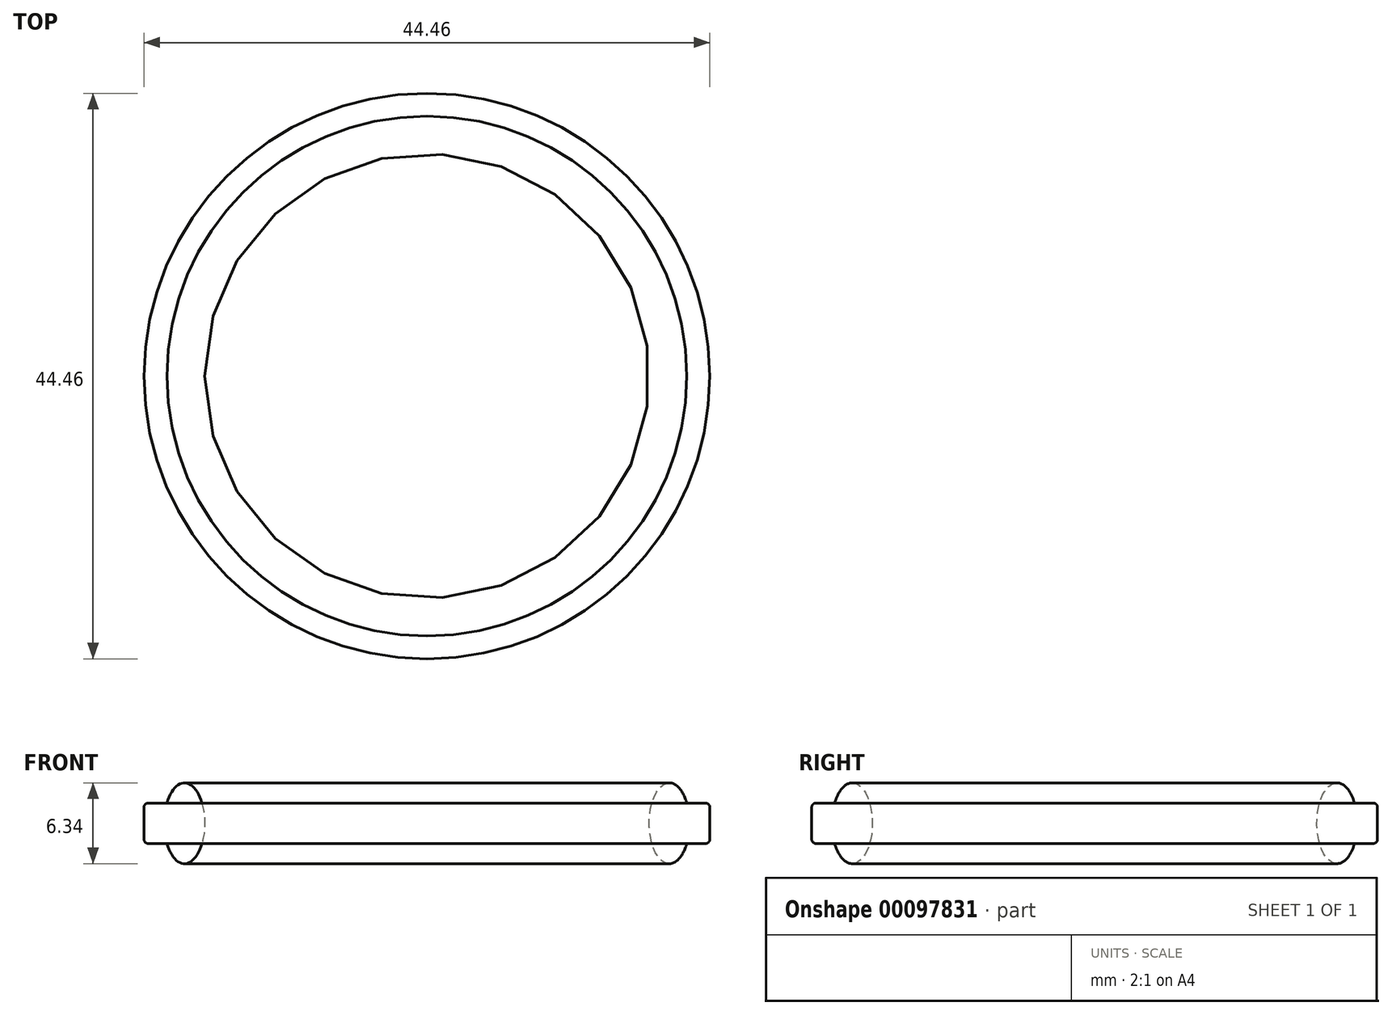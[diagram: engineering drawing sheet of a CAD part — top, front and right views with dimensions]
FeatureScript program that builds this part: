
annotation { "Feature Type Name" : "Feature", "Feature Type Description" : "" }
export const myFeature = defineFeature(function(context is Context, id is Id, definition is map)
    precondition{}
    {
        {
            var Q0;
            Q0=qCreatedBy(makeId("Front.planeOp"),FACE);
            var sketch = newSketch(context, id + "F1", { "sketchPlane" : qUnion([Q0])});
            skEllipticalArc(sketch, "E0", {});
            skLineSegment(sketch, "E1", {"start": v(0, 16.85) * mm, "end": v(0, -16.16) * mm, "construction": true});
            skLineSegment(sketch, "E2.bottom", {"start": v(20.42, 1.59) * mm, "end": v(21.9, 1.59) * mm});
            skLineSegment(sketch, "E2.top", {"start": v(20.42, -1.59) * mm, "end": v(21.9, -1.59) * mm});
            skLineSegment(sketch, "E2.right", {"start": v(22.23, 1.27) * mm, "end": v(22.23, -1.27) * mm});
            skLineSegment(sketch, "E3", {"start": v(22.23, 0) * mm, "end": v(19.05, 0) * mm, "construction": true});
            skPoint(sketch, "E4.visualSharp", {"position": v(22.23, 1.59) * mm});
            skArc(sketch, "E4.filletArc", {"start": v(22.23, 1.27) * mm, "mid": v(22.13, 1.5) * mm, "end": v(21.9, 1.59) * mm});
            skPoint(sketch, "E5.visualSharp", {"position": v(22.23, -1.59) * mm});
            skArc(sketch, "E5.filletArc", {"start": v(21.9, -1.59) * mm, "mid": v(22.13, -1.5) * mm, "end": v(22.23, -1.27) * mm});
            const initialGuessF5lWWFrRyVwqy6wF3_0  = {"E0": [0.01905, 0, 0, -1, 0.003175, 0.0015875000000000002, 2.094395102393195, 1.047197551196597]};
            skSetInitialGuess(sketch, initialGuessF5lWWFrRyVwqy6wF3_0);
            skSolve(sketch);
        }
        {
            var Q0;
            Q0=sQuery(id+"F1.wireOp",EDGE,"E0");
            var Q1;
            Q1=sQuery(id+"F1.wireOp",EDGE,"E2.bottom");
            var Q2;
            Q2=sQuery(id+"F1.wireOp",EDGE,"E4.filletArc");
            var Q3;
            Q3=sQuery(id+"F1.wireOp",EDGE,"E2.right");
            var Q4;
            Q4=sQuery(id+"F1.wireOp",EDGE,"E5.filletArc");
            var Q5;
            Q5=sQuery(id+"F1.wireOp",EDGE,"E2.top");
            var Q6;
            Q6=sQuery(id+"F1.wireOp",EDGE,"E1");
            revolve(context, id + "F0", {"bodyType" : ToolBodyType.SURFACE, "surfaceEntities" : qUnion([Q0, Q1, Q2, Q3, Q4, Q5]), "axis" : qUnion([Q6]), "revolveType" : RevolveType.FULL});
        }
    });
